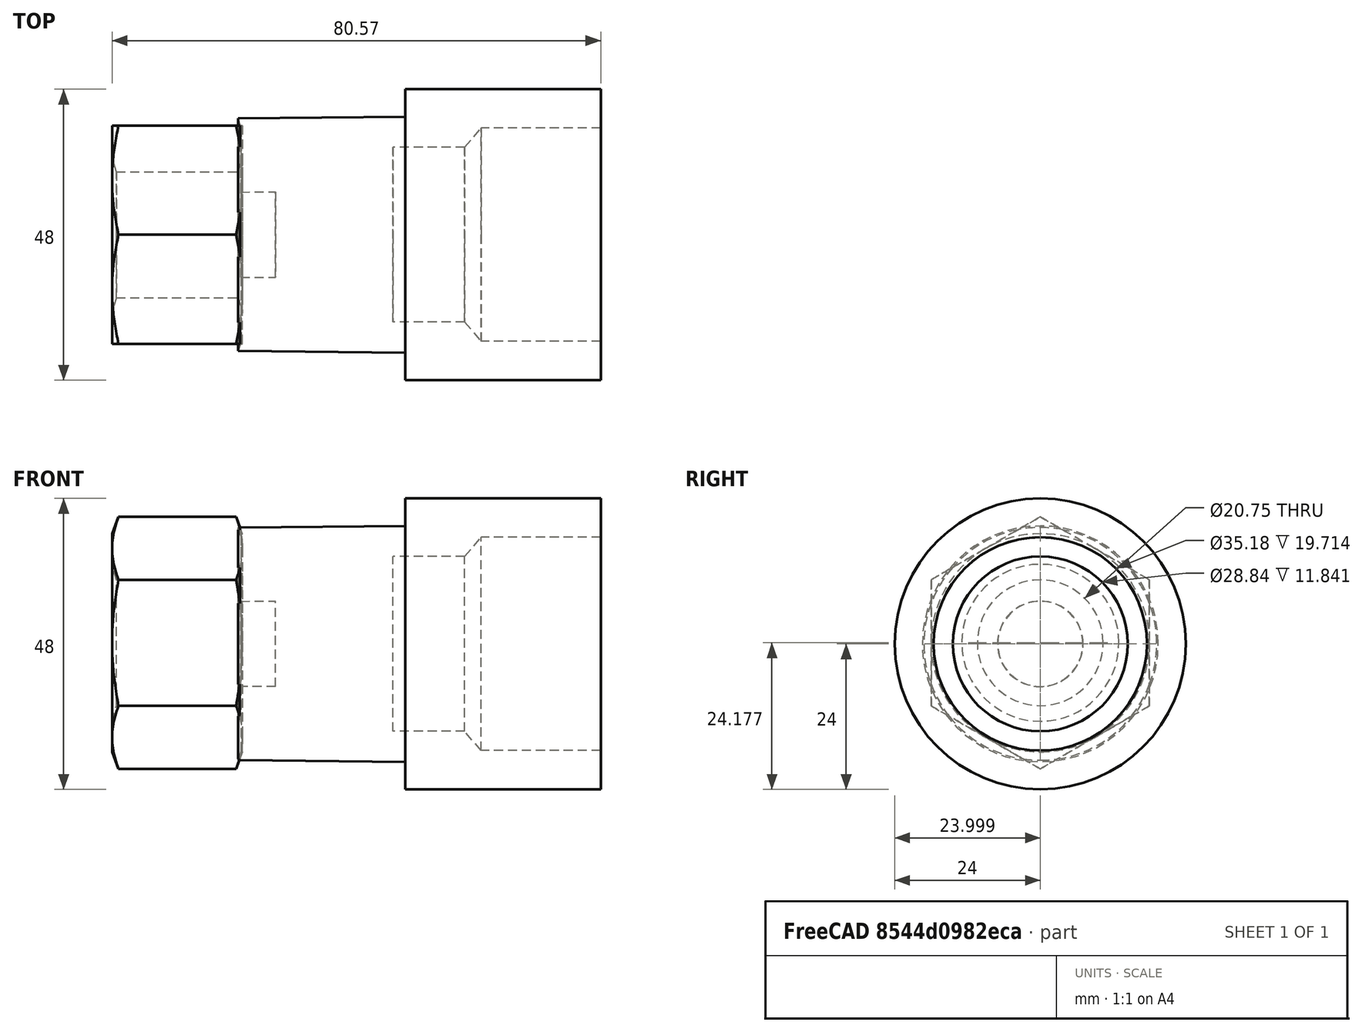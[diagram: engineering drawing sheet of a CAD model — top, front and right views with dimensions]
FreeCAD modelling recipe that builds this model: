
FCSTD DOCUMENT  (FreeCAD 0.16R6706 (Git))
Label: 3_4_quick coupler female
License: All rights reserved
LicenseURL: http://en.wikipedia.org/wiki/All_rights_reserved
objects: Sketcher::SketchObject×2, PartDesign::Revolution×1, Part::FeaturePython×1, Part::MultiFuse×1
note: 6 computed .brp shape members not serialized (recipe doc carries the construction recipe); baked Part::Feature solids carry a one-line shape summary decoded from their .brp

FEATURE [Sketcher::SketchObject] Sketch
  Placement = pos=(0,0,0) rot=(-1,0,0;4.71239rad)
  sketch-geometry (30):
    g0: LineSegment StartX=-42.8542 StartY=-11.2837 StartZ=0 EndX=-40.4667 EndY=-14 EndZ=0
    g1: LineSegment StartX=-28 StartY=-14 StartZ=0 EndX=-40.4667 EndY=-14 EndZ=0
    g2: LineSegment StartX=-28 StartY=-14 StartZ=0 EndX=-28 EndY=-15.9239 EndZ=0
    g3: LineSegment StartX=-28 StartY=-15.9239 StartZ=0 EndX=-24.9718 EndY=-15.9239 EndZ=0
    g4: LineSegment StartX=-24.9718 StartY=-15.9239 StartZ=0 EndX=-23.6546 EndY=-13.9506 EndZ=0
    g5: LineSegment StartX=-23.6546 StartY=-13.9506 StartZ=0 EndX=-19.3015 EndY=-13.9506 EndZ=0
    g6: LineSegment StartX=-19.3015 StartY=-13.9506 StartZ=0 EndX=-17.9936 EndY=-15.778 EndZ=0
    g7: LineSegment StartX=-17.9936 StartY=-15.778 StartZ=0 EndX=-6.21328 EndY=-15.778 EndZ=0
    g8: LineSegment StartX=-6.21328 StartY=-15.778 StartZ=0 EndX=-6.21328 EndY=-17.5332 EndZ=0
    g9: LineSegment StartX=-6.21328 StartY=-17.5332 StartZ=0 EndX=7 EndY=-17.5332 EndZ=0
    g10: LineSegment StartX=-42.8542 StartY=-11.2837 StartZ=0 EndX=-42.8736 EndY=-6.40644 EndZ=0
    g11: LineSegment StartX=7 StartY=-17.5332 StartZ=0 EndX=7 EndY=0 EndZ=0
    g12: LineSegment StartX=-42 StartY=0 StartZ=0 EndX=7 EndY=0 EndZ=0
    g13: LineSegment [constr] StartX=-51.0617 StartY=-2.99968 StartZ=0 EndX=-47.2274 EndY=-2.99968 EndZ=0
    g14: LineSegment [constr] StartX=-47.2274 StartY=-2.99968 StartZ=0 EndX=-47.2274 EndY=-17.4997 EndZ=0
    g15: LineSegment [constr] StartX=-47.2274 StartY=-17.4997 StartZ=0 EndX=-51.0617 EndY=-17.4997 EndZ=0
    g16: LineSegment [constr] StartX=-51.0617 StartY=-17.4997 StartZ=0 EndX=-51.0617 EndY=-2.99968 EndZ=0
    g17: LineSegment [constr] StartX=-42.9595 StartY=9.80413 StartZ=0 EndX=14.0405 EndY=9.80413 EndZ=0
    g18: LineSegment [constr] StartX=14.0405 StartY=9.80413 StartZ=0 EndX=14.0405 EndY=-8.28035 EndZ=0
    g19: LineSegment [constr] StartX=14.0405 StartY=-8.28035 StartZ=0 EndX=-42.9595 EndY=-8.28035 EndZ=0
    g20: LineSegment [constr] StartX=-42.9595 StartY=-8.28035 StartZ=0 EndX=-42.9595 EndY=9.80413 EndZ=0
    g21: LineSegment [constr] StartX=-11.3091 StartY=-0.06637 StartZ=0 EndX=7 EndY=-0.06637 EndZ=0
    g22: LineSegment [constr] StartX=7 StartY=-0.06637 StartZ=0 EndX=7 EndY=-17.5664 EndZ=0
    g23: LineSegment [constr] StartX=7 StartY=-17.5664 StartZ=0 EndX=-11.3091 EndY=-17.5664 EndZ=0
    g24: LineSegment [constr] StartX=-11.3091 StartY=-17.5664 StartZ=0 EndX=-11.3091 EndY=-0.06637 EndZ=0
    g25: LineSegment StartX=-42.8736 StartY=-6.40644 StartZ=0 EndX=-44.9433 EndY=-3.00657 EndZ=0
    g26: LineSegment StartX=-47.1883 StartY=-1.74499 StartZ=0 EndX=-49 EndY=-1.74499 EndZ=0
    g27: ArcOfCircle CenterX=-47.1883 CenterY=-4.37323 CenterZ=0 NormalX=0 NormalY=0 NormalZ=1 Radius=2.62824 StartAngle=0.546842 EndAngle=1.5708
    g28: LineSegment StartX=-49 StartY=-1.74499 StartZ=0 EndX=-49 EndY=0 EndZ=0
    g29: LineSegment StartX=-42 StartY=0 StartZ=0 EndX=-49 EndY=0 EndZ=0
  constraints (58):
    c: Horizontal(g1)
    c: Coincident(g2,g1)
    c: Vertical(g2)
    c: Coincident(g2,g3)
    c: Horizontal(g3)
    c: Coincident(g3,g4)
    c: Coincident(g4,g5)
    c: Horizontal(g5)
    c: Coincident(g5,g6)
    c: Coincident(g6,g7)
    c: Horizontal(g7)
    c: Coincident(g7,g8)
    c: Vertical(g8)
    c: Coincident(g8,g9)
    c: Horizontal(g9)
    c: Coincident(g10,g0)
    c: Coincident(g0,g1)
    c: Vertical(g11)
    c: Coincident(g9,g11)
    c: Coincident(g12,g11)
    c: Horizontal(g12)
    c: Coincident(g13,g14)
    c: Coincident(g14,g15)
    c: Coincident(g15,g16)
    c: Coincident(g16,g13)
    c: Horizontal(g13)
    c: Horizontal(g15)
    c: Vertical(g14)
    c: Vertical(g16)
    c: Distance(g16) = 14.5
    c: Coincident(g17,g18)
    c: Coincident(g18,g19)
    c: Coincident(g19,g20)
    c: Coincident(g20,g17)
    c: Horizontal(g17)
    c: Horizontal(g19)
    c: Vertical(g18)
    c: Vertical(g20)
    c: Distance(g17) = 57
    c: Coincident(g21,g22)
    c: Coincident(g22,g23)
    c: Coincident(g23,g24)
    c: Coincident(g24,g21)
    c: Horizontal(g21)
    c: Horizontal(g23)
    c: Vertical(g22)
    c: Vertical(g24)
    c: Distance(g22) = 17.5
    c: Horizontal(g26)
    c: Tangent(g25,g27) = -1.5708
    c: Tangent(g26,g27) = -1.5708
    c: Coincident(g10,g25)
    c: Coincident(g28,g26)
    c: PointOnObject(g28,g-1)
    c: Vertical(g28)
    c: Coincident(g29,g12)
    c: Coincident(g29,g28)
    c: Horizontal(g29)
FEATURE [Sketcher::SketchObject] Sketch001
  Placement = pos=(0,0,0) rot=(-1,0,0;4.71239rad)
  sketch-geometry (16):
    g0: LineSegment [constr] StartX=-101.712 StartY=24 StartZ=0 EndX=-21.7121 EndY=24 EndZ=0
    g1: LineSegment [constr] StartX=-21.7121 StartY=24 StartZ=0 EndX=-21.7121 EndY=-24 EndZ=0
    g2: LineSegment [constr] StartX=-101.712 StartY=19 StartZ=0 EndX=-53.1714 EndY=19 EndZ=0
    g3: LineSegment StartX=-75.32 StartY=-7.06072 StartZ=0 EndX=-81.0824 EndY=-7.02132 EndZ=0
    g4: LineSegment StartX=-81.0824 StartY=-7.02132 StartZ=0 EndX=-80.9796 EndY=-17.669 EndZ=0
    g5: LineSegment StartX=-80.9796 StartY=-17.669 StartZ=0 EndX=-81.5279 EndY=-19.1906 EndZ=0
    g6: LineSegment StartX=-81.5279 StartY=-19.1906 StartZ=0 EndX=-53.933 EndY=-19.453 EndZ=0
    g7: LineSegment StartX=-53.933 StartY=-19.453 StartZ=0 EndX=-53.933 EndY=-24 EndZ=0
    g8: LineSegment StartX=-53.933 StartY=-24 StartZ=0 EndX=-21.7121 EndY=-24 EndZ=0
    g9: LineSegment StartX=-21.7121 StartY=-24 StartZ=0 EndX=-21.7121 EndY=-17.5891 EndZ=0
    g10: LineSegment StartX=-21.7121 StartY=-17.5891 StartZ=0 EndX=-41.4257 EndY=-17.5891 EndZ=0
    g11: LineSegment StartX=-41.4257 StartY=-17.5891 StartZ=0 EndX=-44.1432 EndY=-14.4186 EndZ=0
    g12: LineSegment StartX=-44.1432 StartY=-14.4186 StartZ=0 EndX=-55.984 EndY=-14.4186 EndZ=0
    g13: LineSegment StartX=-55.984 StartY=-14.4186 StartZ=0 EndX=-55.984 EndY=0 EndZ=0
    g14: LineSegment StartX=-55.984 StartY=0 StartZ=0 EndX=-75.32 EndY=0 EndZ=0
    g15: LineSegment StartX=-75.32 StartY=0 StartZ=0 EndX=-75.32 EndY=-7.06072 EndZ=0
  constraints (29):
    c: Coincident(g0,g1)
    c: Horizontal(g0)
    c: Vertical(g1)
    c: Distance(g1) = 48
    c: DistanceY(g-1,g0) = 24
    c: Horizontal(g2)
    c: DistanceY(g-1,g2) = 19
    c: Coincident(g3,g4)
    c: Coincident(g4,g5)
    c: Coincident(g6,g7)
    c: Vertical(g7)
    c: Coincident(g7,g8)
    c: Coincident(g8,g1)
    c: Coincident(g8,g9)
    c: Vertical(g9)
    c: Coincident(g9,g10)
    c: Horizontal(g10)
    c: Coincident(g10,g11)
    c: Coincident(g11,g12)
    c: Horizontal(g12)
    c: Coincident(g12,g13)
    c: PointOnObject(g13,g-1)
    c: Vertical(g13)
    c: Coincident(g13,g14)
    c: Horizontal(g14)
    c: Coincident(g14,g15)
    c: Coincident(g15,g3)
    c: Vertical(g15)
    c: Coincident(g6,g5)
FEATURE [PartDesign::Revolution] Revolution001
  Angle = 360
  Axis = (1,0,0)
  Base = (0,0,0)
  Placement = pos=(0,0,0) rot=(-1,0,0;4.71239rad)
  ReferenceAxis = -> Sketch001 [H_Axis]
  Reversed = true
  Sketch = -> Sketch001
FEATURE [Part::FeaturePython] Nut001  label="M24-Nut001"  # Fasteners workbench fastener (typed FeaturePython)
  Placement = pos=(-102.282,-0.00060229,0.176504) rot=(0,1,0;1.5708rad)
  diameter = 17
  invert = false
  matchOuter = false
  offset = 0
  thread = false
  type = 1
FEATURE [Part::MultiFuse] Fusion001
  Shapes = -> [Revolution001,Nut001]
